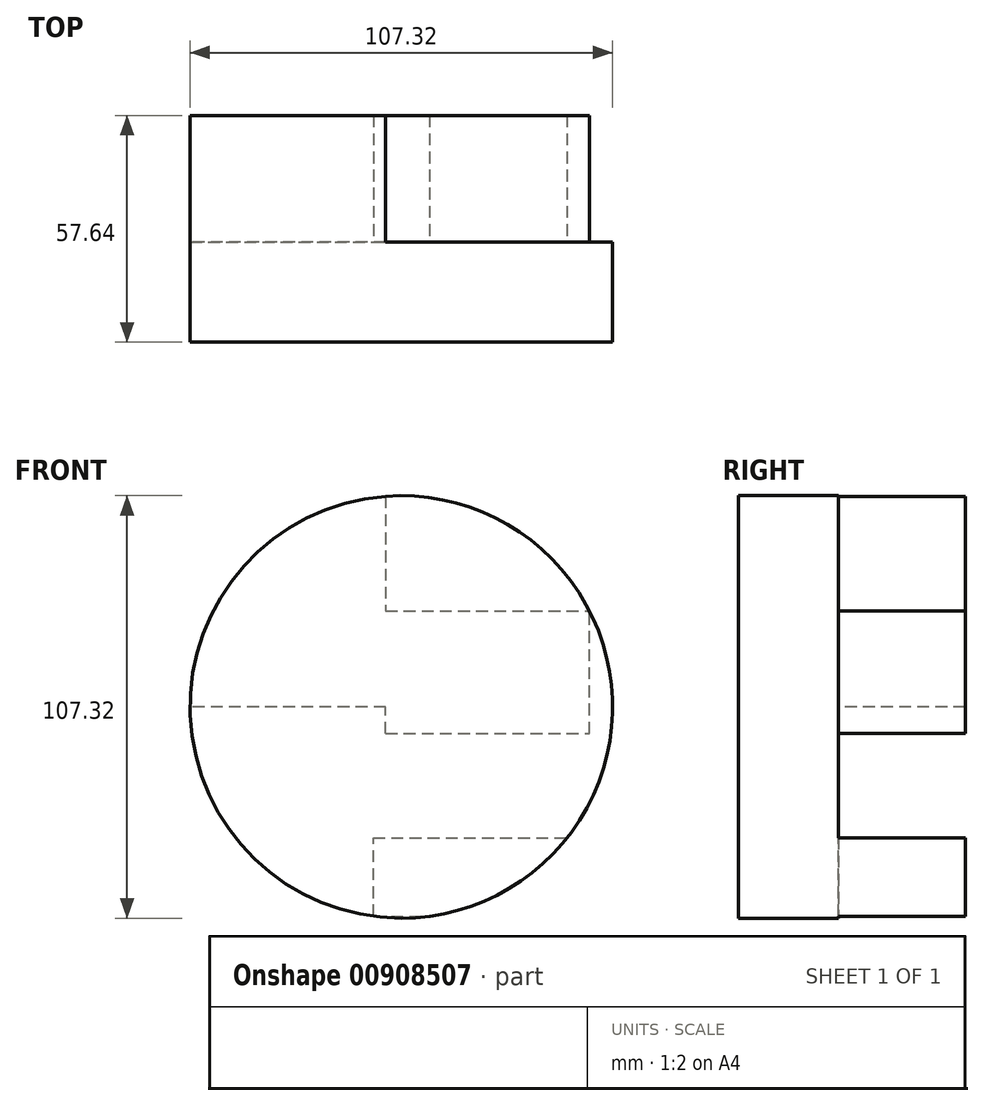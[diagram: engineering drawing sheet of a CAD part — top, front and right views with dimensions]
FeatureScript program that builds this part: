
annotation { "Feature Type Name" : "Feature", "Feature Type Description" : "" }
export const myFeature = defineFeature(function(context is Context, id is Id, definition is map)
    precondition{}
    {
        {
            var Q0;
            Q0=qCreatedBy(makeId("Front.planeOp"),FACE);
            var sketch = newSketch(context, id + "F0", { "sketchPlane" : qUnion([Q0])});
            skCircle(sketch, "E0", {"center": v(53.66, 0) * mm, "radius": 53.66 * mm});
            skSolve(sketch);
        }
        {
            var Q0;
            Q0=makeQuery(id+"F0.imprint","IMPRINT",FACE,{"disambiguationData":[TD([[makeQuery(id+"F0.imprint","IMPRINT",EDGE,{"derivedFrom":sQuery(id+"F0.wireOp",EDGE,"E0")}),1.0]])]});
            extrude(context, id + "F1", {"entities" : qUnion([Q0]), "depth" : 25.4 * mm, "offsetDistance" : 25.4 * mm});
        }
        {
            var Q0;
            Q0=makeQuery(id+"F1.opExtrude","CAP_FACE",FACE,{"disambiguationData":[OSD([sQuery(id+"F0.wireOp",EDGE,"E0")])],"isStart":true});
            var sketch = newSketch(context, id + "F2", { "sketchPlane" : qUnion([Q0])});
            skLineSegment(sketch, "E1.bottom", {"start": v(-49.68, -6.75) * mm, "end": v(-101.48, -6.75) * mm});
            skLineSegment(sketch, "E1.top", {"start": v(-49.68, 24.35) * mm, "end": v(-101.48, 24.35) * mm});
            skLineSegment(sketch, "E1.left", {"start": v(-49.68, -6.75) * mm, "end": v(-49.68, 24.35) * mm});
            skLineSegment(sketch, "E1.right", {"start": v(-101.48, -6.75) * mm, "end": v(-101.48, 24.35) * mm});
            skLineSegment(sketch, "E2.bottom", {"start": v(-11.52, -33.22) * mm, "end": v(-49.68, -33.22) * mm});
            skLineSegment(sketch, "E2.top", {"start": v(-11.52, -6.75) * mm, "end": v(-49.68, -6.75) * mm});
            skLineSegment(sketch, "E2.left", {"start": v(-11.52, -33.22) * mm, "end": v(-11.52, -6.75) * mm});
            skLineSegment(sketch, "E2.right", {"start": v(-49.68, -33.22) * mm, "end": v(-49.68, -6.75) * mm});
            skLineSegment(sketch, "E3.bottom", {"start": v(-49.68, 24.35) * mm, "end": v(-49.68, 24.35) * mm});
            skLineSegment(sketch, "E3.top", {"start": v(-49.68, 24.35) * mm, "end": v(-49.68, 24.35) * mm});
            skLineSegment(sketch, "E3.left", {"start": v(-49.68, 24.35) * mm, "end": v(-49.68, 24.35) * mm});
            skLineSegment(sketch, "E3.right", {"start": v(-49.68, 24.35) * mm, "end": v(-49.68, 24.35) * mm});
            skLineSegment(sketch, "E4.bottom", {"start": v(-49.68, 53.51) * mm, "end": v(0, 53.51) * mm});
            skLineSegment(sketch, "E4.top", {"start": v(-49.68, 0) * mm, "end": v(0, 0) * mm});
            skLineSegment(sketch, "E4.left", {"start": v(-49.68, 53.51) * mm, "end": v(-49.68, 0) * mm});
            skLineSegment(sketch, "E4.right", {"start": v(0, 53.51) * mm, "end": v(0, 0) * mm});
            skLineSegment(sketch, "E5.bottom", {"start": v(-46.56, -53.19) * mm, "end": v(-95.8, -53.19) * mm});
            skLineSegment(sketch, "E5.top", {"start": v(-46.56, -33.22) * mm, "end": v(-95.8, -33.22) * mm});
            skLineSegment(sketch, "E5.left", {"start": v(-46.56, -53.19) * mm, "end": v(-46.56, -33.22) * mm});
            skLineSegment(sketch, "E5.right", {"start": v(-95.8, -53.19) * mm, "end": v(-95.8, -33.22) * mm});
            skSolve(sketch);
        }
        {
            var Q0;
            {var subQ0=sQuery(id+"F2.wireOp",EDGE,"E4.top");Q0=makeQuery(id+"F2.imprint","IMPRINT",FACE,{"disambiguationData":[TD([[makeQuery(id+"F2.imprint","IMPRINT",EDGE,{"derivedFrom":subQ0}),1.0]])]});}
            var Q1;
            Q1=makeQuery(id+"F2.imprint","IMPRINT",FACE,{"disambiguationData":[TD([[makeQuery(id+"F2.imprint","IMPRINT",EDGE,{"derivedFrom":sQuery(id+"F2.wireOp",EDGE,"E1.bottom")}),-1.0]])]});
            var Q2;
            {var subQ0=sQuery(id+"F2.wireOp",EDGE,"E5.left");Q2=makeQuery(id+"F2.imprint","IMPRINT",FACE,{"disambiguationData":[TD([[makeQuery(id+"F2.imprint","IMPRINT",EDGE,{"derivedFrom":subQ0}),1.0]])]});}
            extrude(context, id + "F3", {"entities" : qUnion([Q0, Q1, Q2]), "operationType" : NewBodyOperationType.ADD, "depth" : 32.24 * mm, "offsetDistance" : 25.4 * mm});
        }
    });
